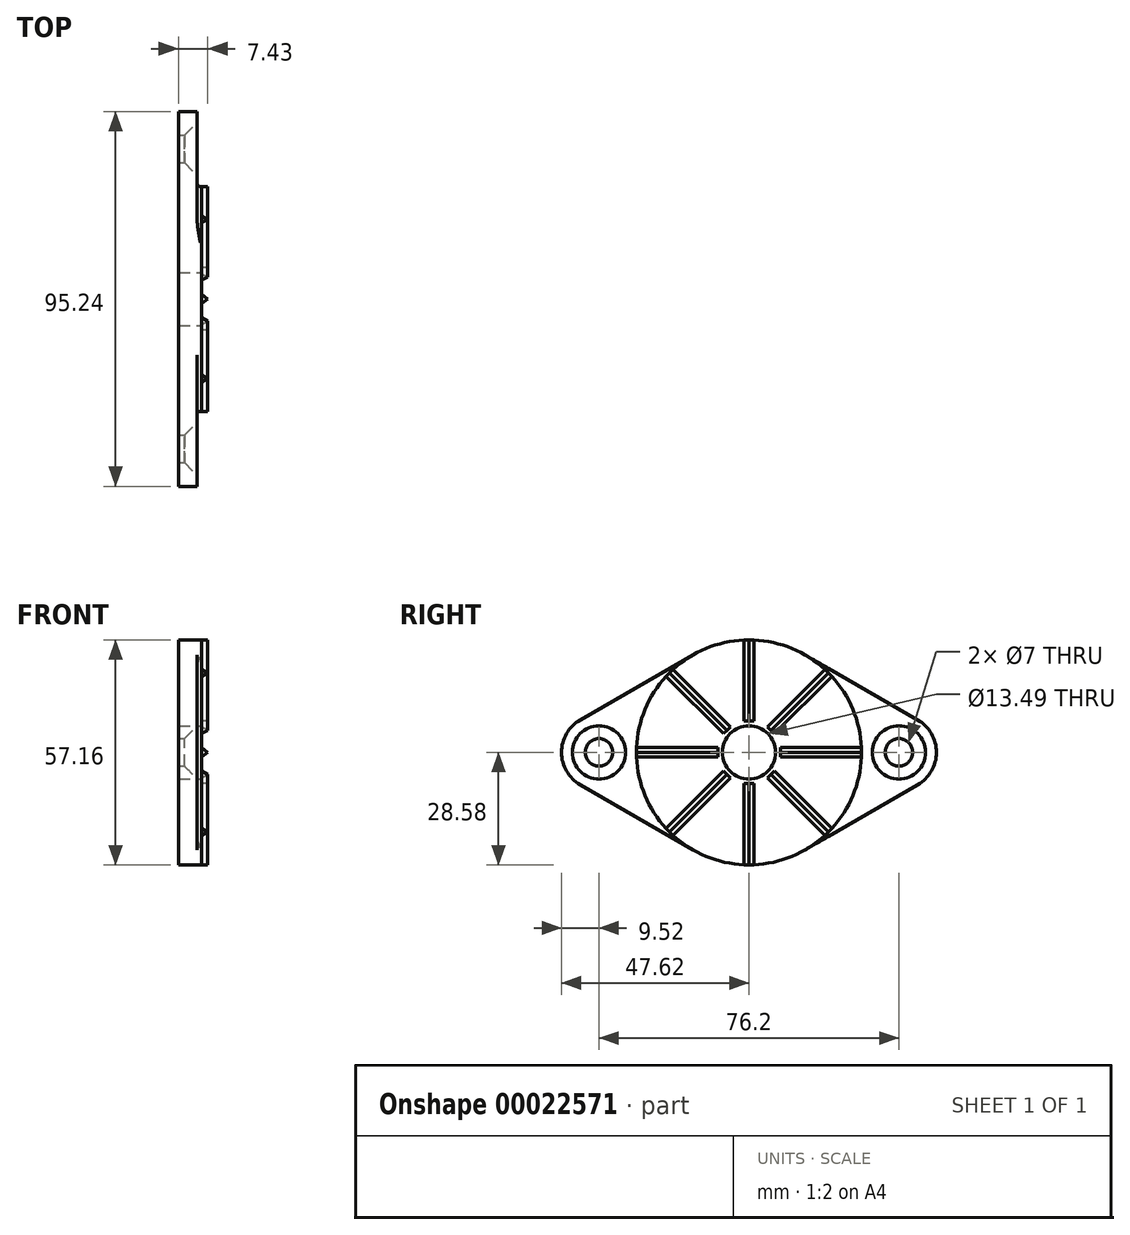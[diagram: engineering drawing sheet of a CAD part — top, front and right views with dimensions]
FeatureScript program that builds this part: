
annotation { "Feature Type Name" : "Feature", "Feature Type Description" : "" }
export const myFeature = defineFeature(function(context is Context, id is Id, definition is map)
    precondition{}
    {
        {
            var Q0;
            Q0=qCreatedBy(makeId("Right.planeOp"),FACE);
            var sketch = newSketch(context, id + "F0", { "sketchPlane" : qUnion([Q0])});
            skArc(sketch, "E0", {"start": v(-14.29, -24.75) * mm, "mid": v(0, -28.58) * mm, "end": v(14.29, -24.75) * mm});
            skLineSegment(sketch, "E1", {"start": v(-77.57, 0) * mm, "end": v(77.57, 0) * mm, "construction": true});
            skArc(sketch, "E2", {"start": v(-42.86, 8.25) * mm, "mid": v(-47.62, 0) * mm, "end": v(-42.86, -8.25) * mm});
            skArc(sketch, "E3", {"start": v(42.86, -8.25) * mm, "mid": v(47.62, 0) * mm, "end": v(42.86, 8.25) * mm});
            skLineSegment(sketch, "E4", {"start": v(-42.86, 8.25) * mm, "end": v(-14.29, 24.75) * mm});
            skLineSegment(sketch, "E5", {"start": v(-42.86, -8.25) * mm, "end": v(-14.29, -24.75) * mm});
            skLineSegment(sketch, "E6", {"start": v(42.86, -8.25) * mm, "end": v(14.29, -24.75) * mm});
            skLineSegment(sketch, "E7", {"start": v(42.86, 8.25) * mm, "end": v(14.29, 24.75) * mm});
            skArc(sketch, "E8.trimOffspring", {"start": v(14.29, 24.75) * mm, "mid": v(0, 28.57) * mm, "end": v(-14.29, 24.75) * mm});
            skSolve(sketch);
        }
        {
            var Q0;
            Q0=qSketchRegion(id+"F0",true);
            extrude(context, id + "F1", {"entities" : qUnion([Q0]), "depth" : 4.76 * mm});
        }
        {
            var Q0;
            Q0=makeQuery(id+"F1.opExtrude","CAP_FACE",FACE,{"disambiguationData":[OSD([sQuery(id+"F0.wireOp",EDGE,"E0"),sQuery(id+"F0.wireOp",EDGE,"E2"),sQuery(id+"F0.wireOp",EDGE,"E3"),sQuery(id+"F0.wireOp",EDGE,"E4"),sQuery(id+"F0.wireOp",EDGE,"E5"),sQuery(id+"F0.wireOp",EDGE,"E6"),sQuery(id+"F0.wireOp",EDGE,"E7"),sQuery(id+"F0.wireOp",EDGE,"E8.trimOffspring")])],"isStart":false});
            var sketch = newSketch(context, id + "F2", { "sketchPlane" : qUnion([Q0])});
            skCircle(sketch, "E9", {"center": v(0, 0) * mm, "radius": 28.58 * mm});
            skSolve(sketch);
        }
        {
            var Q0;
            Q0=qSketchRegion(id+"F2",true);
            extrude(context, id + "F3", {"entities" : qUnion([Q0]), "operationType" : NewBodyOperationType.ADD, "depth" : 1.08 * mm});
        }
        {
            var Q0;
            Q0=qCreatedBy(makeId("Top.planeOp"),FACE);
            cPlane(context, id + "F4", {"entities" : qUnion([Q0]), "cplaneType" : CPlaneType.OFFSET, "offset" : 28.57 * mm, "width" : 152.4 * mm, "height" : 152.4 * mm});
        }
        {
            var Q0;
            Q0=qCreatedBy(makeId("Top.planeOp"),FACE);
            cPlane(context, id + "F5", {"entities" : qUnion([Q0]), "cplaneType" : CPlaneType.OFFSET, "offset" : 7.94 * mm, "width" : 152.4 * mm, "height" : 152.4 * mm});
        }
        {
            var Q0;
            Q0=qCreatedBy(id+"F4.planeOp",FACE);
            var sketch = newSketch(context, id + "F6", { "sketchPlane" : qUnion([Q0])});
            skLineSegment(sketch, "E10", {"start": v(0, 0) * mm, "end": v(5.84, 0) * mm, "construction": true});
            skLineSegment(sketch, "E11", {"start": v(5.84, 1.22) * mm, "end": v(5.84, -1.22) * mm});
            skLineSegment(sketch, "E12", {"start": v(5.84, 0) * mm, "end": v(7.43, 0) * mm, "construction": true});
            skLineSegment(sketch, "E13", {"start": v(5.84, -1.22) * mm, "end": v(7.43, 0) * mm});
            skLineSegment(sketch, "E14", {"start": v(5.84, 1.22) * mm, "end": v(7.43, 0) * mm});
            skSolve(sketch);
        }
        {
            var Q0;
            Q0=qCreatedBy(id+"F5.planeOp",FACE);
            var sketch = newSketch(context, id + "F7", { "sketchPlane" : qUnion([Q0])});
            skLineSegment(sketch, "E15", {"start": v(5.84, -1.22) * mm, "end": v(5.84, 1.22) * mm});
            skLineSegment(sketch, "E16", {"start": v(-1.93, 0) * mm, "end": v(5.84, 0) * mm, "construction": true});
            skLineSegment(sketch, "E17", {"start": v(5.84, 0) * mm, "end": v(7.43, 0) * mm, "construction": true});
            skLineSegment(sketch, "E18", {"start": v(5.84, -1.22) * mm, "end": v(7.43, 0) * mm});
            skLineSegment(sketch, "E19", {"start": v(7.43, 0) * mm, "end": v(5.84, 1.22) * mm});
            skSolve(sketch);
        }
        {
            var Q1;
            Q1=qSketchRegion(id+"F7",true);
            var Q2;
            Q2=qSketchRegion(id+"F6",true);
            loft(context, id + "F8", {"operationType" : NewBodyOperationType.ADD, "sheetProfilesArray" : [{ "sheetProfileEntities" : qUnion([Q1]) }, { "sheetProfileEntities" : qUnion([Q2]) }]});
        }
        {
            var Q0;
            {var subQ0=sQuery(id+"F6.wireOp",EDGE,"E11");var subQ1=sQuery(id+"F6.wireOp",EDGE,"E13");var subQ2=sQuery(id+"F6.wireOp",EDGE,"E14");var subQ3=sQuery(id+"F7.wireOp",EDGE,"E15");var subQ4=sQuery(id+"F7.wireOp",EDGE,"E18");var subQ5=sQuery(id+"F7.wireOp",EDGE,"E19");Q0=makeQuery(id+"F8.opLoft","SWEPT_FACE",FACE,{"disambiguationData":[OSD([subQ0,subQ1,subQ2,subQ3,subQ4,subQ5]),TDD([makeQuery(id+"F6.imprint","INTERSECT",VERTEX,{"derivedFrom":[subQ0,subQ2]}),makeQuery(id+"F6.imprint","INTERSECT",VERTEX,{"derivedFrom":[subQ1,subQ2]}),makeQuery(id+"F6.imprint","IMPRINT",EDGE,{"derivedFrom":subQ2}),makeQuery(id+"F7.imprint","INTERSECT",VERTEX,{"derivedFrom":[subQ3,subQ4]}),makeQuery(id+"F7.imprint","INTERSECT",VERTEX,{"derivedFrom":[subQ4,subQ5]}),makeQuery(id+"F7.imprint","IMPRINT",EDGE,{"derivedFrom":subQ4})])]});}
            var Q1;
            {var subQ0=sQuery(id+"F6.wireOp",EDGE,"E11");var subQ1=sQuery(id+"F6.wireOp",EDGE,"E13");var subQ2=sQuery(id+"F6.wireOp",EDGE,"E14");var subQ3=sQuery(id+"F7.wireOp",EDGE,"E15");var subQ4=sQuery(id+"F7.wireOp",EDGE,"E18");var subQ5=sQuery(id+"F7.wireOp",EDGE,"E19");Q1=makeQuery(id+"F8.opLoft","SWEPT_FACE",FACE,{"disambiguationData":[OSD([subQ0,subQ1,subQ2,subQ3,subQ4,subQ5]),TDD([makeQuery(id+"F6.imprint","INTERSECT",VERTEX,{"derivedFrom":[subQ0,subQ1]}),makeQuery(id+"F6.imprint","INTERSECT",VERTEX,{"derivedFrom":[subQ1,subQ2]}),makeQuery(id+"F6.imprint","IMPRINT",EDGE,{"derivedFrom":subQ1}),makeQuery(id+"F7.imprint","INTERSECT",VERTEX,{"derivedFrom":[subQ3,subQ5]}),makeQuery(id+"F7.imprint","INTERSECT",VERTEX,{"derivedFrom":[subQ4,subQ5]}),makeQuery(id+"F7.imprint","IMPRINT",EDGE,{"derivedFrom":subQ5})])]});}
            var Q2;
            Q2=makeQuery(id+"F8.opLoft","CAP_FACE",FACE,{"disambiguationData":[OSD([makeQuery(id+"F7.imprint","IMPRINT",FACE,{"disambiguationData":[TD([[makeQuery(id+"F7.imprint","IMPRINT",EDGE,{"derivedFrom":sQuery(id+"F7.wireOp",EDGE,"E15")}),-1.0]])]})])],"isStart":true});
            var Q3;
            Q3=makeQuery(id+"F8.opLoft","CAP_FACE",FACE,{"disambiguationData":[OSD([makeQuery(id+"F6.imprint","IMPRINT",FACE,{"disambiguationData":[TD([[makeQuery(id+"F6.imprint","IMPRINT",EDGE,{"derivedFrom":sQuery(id+"F6.wireOp",EDGE,"E11")}),1.0]])]})])],"isStart":true});
            var Q4;
            {var subQ0=sQuery(id+"F6.wireOp",EDGE,"E11");var subQ1=sQuery(id+"F6.wireOp",EDGE,"E13");var subQ2=sQuery(id+"F6.wireOp",EDGE,"E14");var subQ3=sQuery(id+"F7.wireOp",EDGE,"E15");var subQ4=sQuery(id+"F7.wireOp",EDGE,"E18");var subQ5=sQuery(id+"F7.wireOp",EDGE,"E19");var subQ6=makeQuery(id+"F6.imprint","INTERSECT",VERTEX,{"derivedFrom":[subQ0,subQ2]});var subQ7=makeQuery(id+"F6.imprint","IMPRINT",EDGE,{"derivedFrom":subQ0});var subQ8=makeQuery(id+"F7.imprint","INTERSECT",VERTEX,{"derivedFrom":[subQ3,subQ4]});var subQ9=makeQuery(id+"F8.opLoft","SWEPT_FACE",FACE,{"disambiguationData":[OSD([subQ0,subQ1,subQ2,subQ3,subQ4,subQ5]),TDD([subQ6,makeQuery(id+"F6.imprint","INTERSECT",VERTEX,{"derivedFrom":[subQ0,subQ1]}),subQ7,makeQuery(id+"F7.imprint","INTERSECT",VERTEX,{"derivedFrom":[subQ3,subQ5]}),subQ8,makeQuery(id+"F7.imprint","IMPRINT",EDGE,{"derivedFrom":subQ3})])]});var subQ10=makeQuery(id+"F6.imprint","IMPRINT",EDGE,{"derivedFrom":subQ2});Q4=makeQuery(id+"F8.boolean.opBoolean","SPLIT",FACE,{"disambiguationData":[TD([makeQuery(id+"F8.opLoft","SWEPT_FACE",FACE,{"disambiguationData":[OSD([subQ0,subQ1,subQ2,subQ3,subQ4,subQ5]),TDD([subQ6,makeQuery(id+"F6.imprint","INTERSECT",VERTEX,{"derivedFrom":[subQ1,subQ2]}),subQ10,subQ8,makeQuery(id+"F7.imprint","INTERSECT",VERTEX,{"derivedFrom":[subQ4,subQ5]}),makeQuery(id+"F7.imprint","IMPRINT",EDGE,{"derivedFrom":subQ4})])]})])],"derivedFrom":subQ9});}
            var Q5;
            {var subQ0=sQuery(id+"F6.wireOp",EDGE,"E11");var subQ1=sQuery(id+"F6.wireOp",EDGE,"E13");var subQ2=sQuery(id+"F6.wireOp",EDGE,"E14");var subQ3=sQuery(id+"F7.wireOp",EDGE,"E15");var subQ4=sQuery(id+"F7.wireOp",EDGE,"E18");var subQ5=sQuery(id+"F7.wireOp",EDGE,"E19");var subQ6=makeQuery(id+"F6.imprint","INTERSECT",VERTEX,{"derivedFrom":[subQ0,subQ1]});var subQ7=makeQuery(id+"F6.imprint","IMPRINT",EDGE,{"derivedFrom":subQ0});var subQ8=makeQuery(id+"F7.imprint","INTERSECT",VERTEX,{"derivedFrom":[subQ3,subQ5]});var subQ9=makeQuery(id+"F8.opLoft","SWEPT_FACE",FACE,{"disambiguationData":[OSD([subQ0,subQ1,subQ2,subQ3,subQ4,subQ5]),TDD([makeQuery(id+"F6.imprint","INTERSECT",VERTEX,{"derivedFrom":[subQ0,subQ2]}),subQ6,subQ7,subQ8,makeQuery(id+"F7.imprint","INTERSECT",VERTEX,{"derivedFrom":[subQ3,subQ4]}),makeQuery(id+"F7.imprint","IMPRINT",EDGE,{"derivedFrom":subQ3})])]});var subQ10=makeQuery(id+"F6.imprint","IMPRINT",EDGE,{"derivedFrom":subQ1});Q5=makeQuery(id+"F8.boolean.opBoolean","SPLIT",FACE,{"disambiguationData":[TD([makeQuery(id+"F8.opLoft","SWEPT_FACE",FACE,{"disambiguationData":[OSD([subQ0,subQ1,subQ2,subQ3,subQ4,subQ5]),TDD([subQ6,makeQuery(id+"F6.imprint","INTERSECT",VERTEX,{"derivedFrom":[subQ1,subQ2]}),subQ10,subQ8,makeQuery(id+"F7.imprint","INTERSECT",VERTEX,{"derivedFrom":[subQ4,subQ5]}),makeQuery(id+"F7.imprint","IMPRINT",EDGE,{"derivedFrom":subQ5})])]})])],"derivedFrom":subQ9});}
            var Q6;
            Q6=makeQuery(id+"F3.boolean.opBoolean","MERGE",FACE,{"derivedFrom":[makeQuery(id+"F1.opExtrude","SWEPT_FACE",FACE,{"disambiguationData":[OSD([sQuery(id+"F0.wireOp",EDGE,"E0")])]}),makeQuery(id+"F1.opExtrude","SWEPT_FACE",FACE,{"disambiguationData":[OSD([sQuery(id+"F0.wireOp",EDGE,"E8.trimOffspring")])]}),makeQuery(id+"F3.opExtrude","SWEPT_FACE",FACE,{"disambiguationData":[OSD([sQuery(id+"F2.wireOp",EDGE,"E9")])]})]});
            circularPattern(context, id + "F9", {"operationType" : NewBodyOperationType.ADD, "faces" : qUnion([Q0, Q1, Q2, Q3, Q4, Q5]), "axis" : qUnion([Q6]), "angle" : 360 * degree, "instanceCount" : 8, "equalSpace" : true, "patternType" : PatternType.FACE});
        }
        {
            var Q0;
            {var subQ0=sQuery(id+"F0.wireOp",EDGE,"E0");var subQ1=sQuery(id+"F0.wireOp",EDGE,"E3");var subQ2=sQuery(id+"F0.wireOp",EDGE,"E6");var subQ3=sQuery(id+"F0.wireOp",EDGE,"E7");var subQ4=sQuery(id+"F0.wireOp",EDGE,"E8.trimOffspring");Q0=makeQuery(id+"F3.boolean.opBoolean","SPLIT",FACE,{"disambiguationData":[TD([makeQuery(id+"F1.opExtrude","SWEPT_FACE",FACE,{"disambiguationData":[OSD([subQ1])]})])],"derivedFrom":makeQuery(id+"F1.opExtrude","CAP_FACE",FACE,{"disambiguationData":[OSD([subQ0,sQuery(id+"F0.wireOp",EDGE,"E2"),subQ1,sQuery(id+"F0.wireOp",EDGE,"E4"),sQuery(id+"F0.wireOp",EDGE,"E5"),subQ2,subQ3,subQ4])],"isStart":false})});}
            var sketch = newSketch(context, id + "F10", { "sketchPlane" : qUnion([Q0])});
            skCircle(sketch, "E20", {"center": v(38.1, 0) * mm, "radius": 3.5 * mm});
            skCircle(sketch, "E21", {"center": v(-38.1, 0) * mm, "radius": 3.5 * mm});
            skCircle(sketch, "E22", {"center": v(0, 0) * mm, "radius": 6.75 * mm});
            skSolve(sketch);
        }
        {
            var Q0;
            Q0=qSketchRegion(id+"F10",true);
            extrude(context, id + "F11", {"entities" : qUnion([Q0]), "operationType" : NewBodyOperationType.REMOVE, "endBound" : BoundingType.SYMMETRIC, "oppositeDirection" : true, "depth" : 25.4 * mm});
        }
        {
            var Q0;
            Q0=makeQuery(id+"F10.imprint","IMPRINT",FACE,{"disambiguationData":[TD([[makeQuery(id+"F10.imprint","IMPRINT",EDGE,{"derivedFrom":sQuery(id+"F10.wireOp",EDGE,"E20")}),-1.0]])]});
            var sketch = newSketch(context, id + "F12", { "sketchPlane" : qUnion([Q0])});
            skCircle(sketch, "E23", {"center": v(38.1, 0) * mm, "radius": 6.75 * mm});
            skCircle(sketch, "E24", {"center": v(-38.1, 0) * mm, "radius": 6.75 * mm});
            skSolve(sketch);
        }
        {
            var Q0;
            Q0=qSketchRegion(id+"F12",true);
            extrude(context, id + "F13", {"entities" : qUnion([Q0]), "operationType" : NewBodyOperationType.REMOVE, "oppositeDirection" : true, "depth" : 25.4 * mm, "hasDraft" : true, "draftAngle" : 45 * degree, "draftPullDirection" : true});
        }
        {
            var Q0;
            {var subQ0=sQuery(id+"F2.wireOp",EDGE,"E9");var subQ3=sQuery(id+"F0.wireOp",EDGE,"E6");Q0=makeQuery(id+"F3.boolean.opBoolean","SPLIT",EDGE,{"disambiguationData":[TD([makeQuery(id+"F1.opExtrude","SWEPT_FACE",FACE,{"disambiguationData":[OSD([subQ3])]})])],"derivedFrom":makeQuery(id+"F3.opExtrude","CAP_EDGE",EDGE,{"disambiguationData":[OSD([subQ0])],"isStart":true})});}
            var Q1;
            {var subQ0=sQuery(id+"F2.wireOp",EDGE,"E9");var subQ3=sQuery(id+"F0.wireOp",EDGE,"E4");Q1=makeQuery(id+"F3.boolean.opBoolean","SPLIT",EDGE,{"disambiguationData":[TD([makeQuery(id+"F1.opExtrude","SWEPT_FACE",FACE,{"disambiguationData":[OSD([subQ3])]})])],"derivedFrom":makeQuery(id+"F3.opExtrude","CAP_EDGE",EDGE,{"disambiguationData":[OSD([subQ0])],"isStart":true})});}
            fillet(context, id + "F14", {"entities" : qUnion([Q0, Q1]), "radius" : 0.8 * mm, "allowEdgeOverflow" : false});
        }
    });
